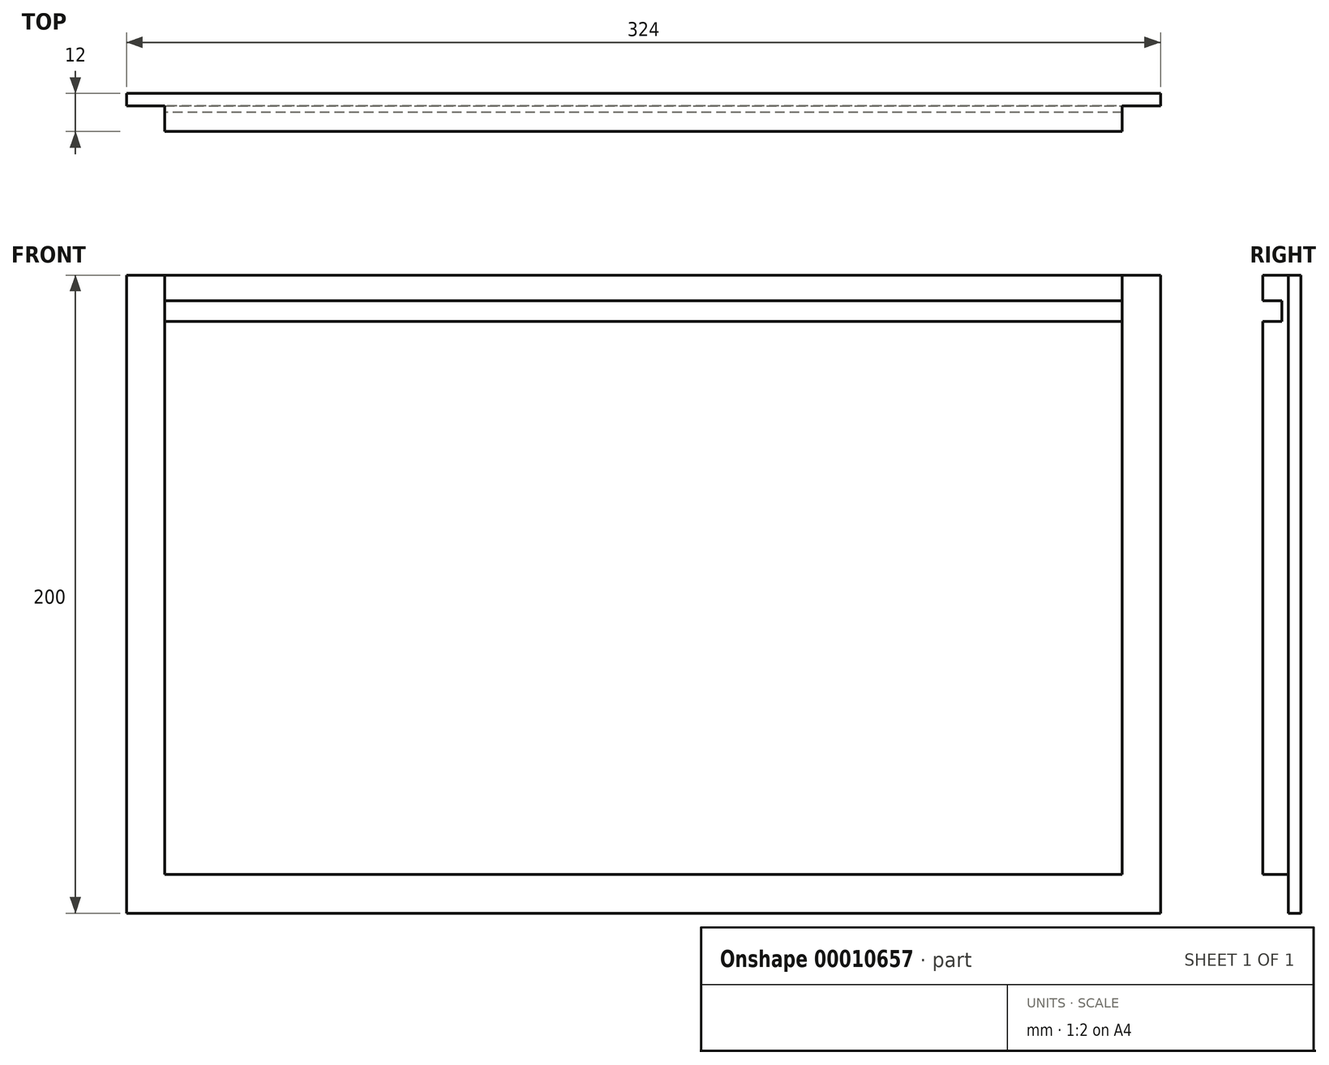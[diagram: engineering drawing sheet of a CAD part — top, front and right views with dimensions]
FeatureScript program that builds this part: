
annotation { "Feature Type Name" : "Feature", "Feature Type Description" : "" }
export const myFeature = defineFeature(function(context is Context, id is Id, definition is map)
    precondition{}
    {
        {
            var Q0;
            Q0=qCreatedBy(makeId("Top.planeOp"),FACE);
            var sketch = newSketch(context, id + "F0", { "sketchPlane" : qUnion([Q0])});
            skLineSegment(sketch, "E0", {"start": v(0, 0) * mm, "end": v(12, 0) * mm});
            skLineSegment(sketch, "E1", {"start": v(12, 0) * mm, "end": v(12, 8) * mm});
            skLineSegment(sketch, "E2", {"start": v(12, 8) * mm, "end": v(312, 8) * mm});
            skLineSegment(sketch, "E3", {"start": v(312, 8) * mm, "end": v(312, 0) * mm});
            skLineSegment(sketch, "E4", {"start": v(312, 0) * mm, "end": v(324, 0) * mm});
            skLineSegment(sketch, "E5", {"start": v(324, 0) * mm, "end": v(324, -4) * mm});
            skLineSegment(sketch, "E6", {"start": v(324, -4) * mm, "end": v(0, -4) * mm});
            skLineSegment(sketch, "E7", {"start": v(0, -4) * mm, "end": v(0, 0) * mm});
            skSolve(sketch);
        }
        {
            var Q0;
            Q0=makeQuery(id+"F0.imprint","IMPRINT",FACE,{"disambiguationData":[TD([[makeQuery(id+"F0.imprint","IMPRINT",EDGE,{"derivedFrom":sQuery(id+"F0.wireOp",EDGE,"E0")}),-1.0]])]});
            extrude(context, id + "F1", {"entities" : qUnion([Q0]), "depth" : 200 * mm});
        }
        {
            var Q0;
            Q0=makeQuery(id+"F1.opExtrude","SWEPT_FACE",FACE,{"disambiguationData":[OSD([sQuery(id+"F0.wireOp",EDGE,"E2")])]});
            var sketch = newSketch(context, id + "F2", { "sketchPlane" : qUnion([Q0])});
            skLineSegment(sketch, "E8.bottom", {"start": v(-12, 192) * mm, "end": v(-312, 192) * mm});
            skLineSegment(sketch, "E8.top", {"start": v(-12, 185.5) * mm, "end": v(-312, 185.5) * mm});
            skLineSegment(sketch, "E8.left", {"start": v(-12, 192) * mm, "end": v(-12, 185.5) * mm});
            skLineSegment(sketch, "E8.right", {"start": v(-312, 192) * mm, "end": v(-312, 185.5) * mm});
            skSolve(sketch);
        }
        {
            var Q0;
            Q0=makeQuery(id+"F2.imprint","IMPRINT",FACE,{"disambiguationData":[TD([[makeQuery(id+"F2.imprint","IMPRINT",EDGE,{"derivedFrom":sQuery(id+"F2.wireOp",EDGE,"E8.bottom")}),1.0]])]});
            extrude(context, id + "F3", {"entities" : qUnion([Q0]), "operationType" : NewBodyOperationType.REMOVE, "oppositeDirection" : true, "depth" : 6 * mm});
        }
        {
            var Q0;
            Q0=makeQuery(id+"F1.opExtrude","CAP_FACE",FACE,{"disambiguationData":[OSD([sQuery(id+"F0.wireOp",EDGE,"E0"),sQuery(id+"F0.wireOp",EDGE,"E1"),sQuery(id+"F0.wireOp",EDGE,"E2"),sQuery(id+"F0.wireOp",EDGE,"E3"),sQuery(id+"F0.wireOp",EDGE,"E4"),sQuery(id+"F0.wireOp",EDGE,"E5"),sQuery(id+"F0.wireOp",EDGE,"E6"),sQuery(id+"F0.wireOp",EDGE,"E7")])],"isStart":true});
            var sketch = newSketch(context, id + "F4", { "sketchPlane" : qUnion([Q0])});
            skLineSegment(sketch, "E9.bottom", {"start": v(312, -8) * mm, "end": v(12, -8) * mm});
            skLineSegment(sketch, "E9.top", {"start": v(312, 0) * mm, "end": v(12, 0) * mm});
            skLineSegment(sketch, "E9.left", {"start": v(312, -8) * mm, "end": v(312, 0) * mm});
            skLineSegment(sketch, "E9.right", {"start": v(12, -8) * mm, "end": v(12, 0) * mm});
            skSolve(sketch);
        }
        {
            var Q0;
            Q0=makeQuery(id+"F4.imprint","IMPRINT",FACE,{"disambiguationData":[TD([[makeQuery(id+"F4.imprint","IMPRINT",EDGE,{"derivedFrom":sQuery(id+"F4.wireOp",EDGE,"E9.bottom")}),1.0]])]});
            extrude(context, id + "F5", {"entities" : qUnion([Q0]), "operationType" : NewBodyOperationType.REMOVE, "oppositeDirection" : true, "depth" : 12.2 * mm});
        }
        {
            var Q0;
            Q0=makeQuery(id+"F1.opExtrude","SWEPT_BODY",BODY,{"disambiguationData":[OSD([sQuery(id+"F0.wireOp",EDGE,"E0"),sQuery(id+"F0.wireOp",EDGE,"E1"),sQuery(id+"F0.wireOp",EDGE,"E2"),sQuery(id+"F0.wireOp",EDGE,"E3"),sQuery(id+"F0.wireOp",EDGE,"E4"),sQuery(id+"F0.wireOp",EDGE,"E5"),sQuery(id+"F0.wireOp",EDGE,"E6"),sQuery(id+"F0.wireOp",EDGE,"E7")])]});
            var Q1;
            Q1=makeQuery(id+"F1.opExtrude","SWEPT_EDGE",EDGE,{"disambiguationData":[OSD([sQuery(id+"F0.wireOp",EDGE,"E0"),sQuery(id+"F0.wireOp",EDGE,"E7")])]});
            transform(context, id + "F6", {"entities" : qUnion([Q0]), "transformType" : TransformType.ROTATION, "transformAxis" : qUnion([Q1]), "angle" : 180 * degree, "makeCopy" : false});
        }
    });
